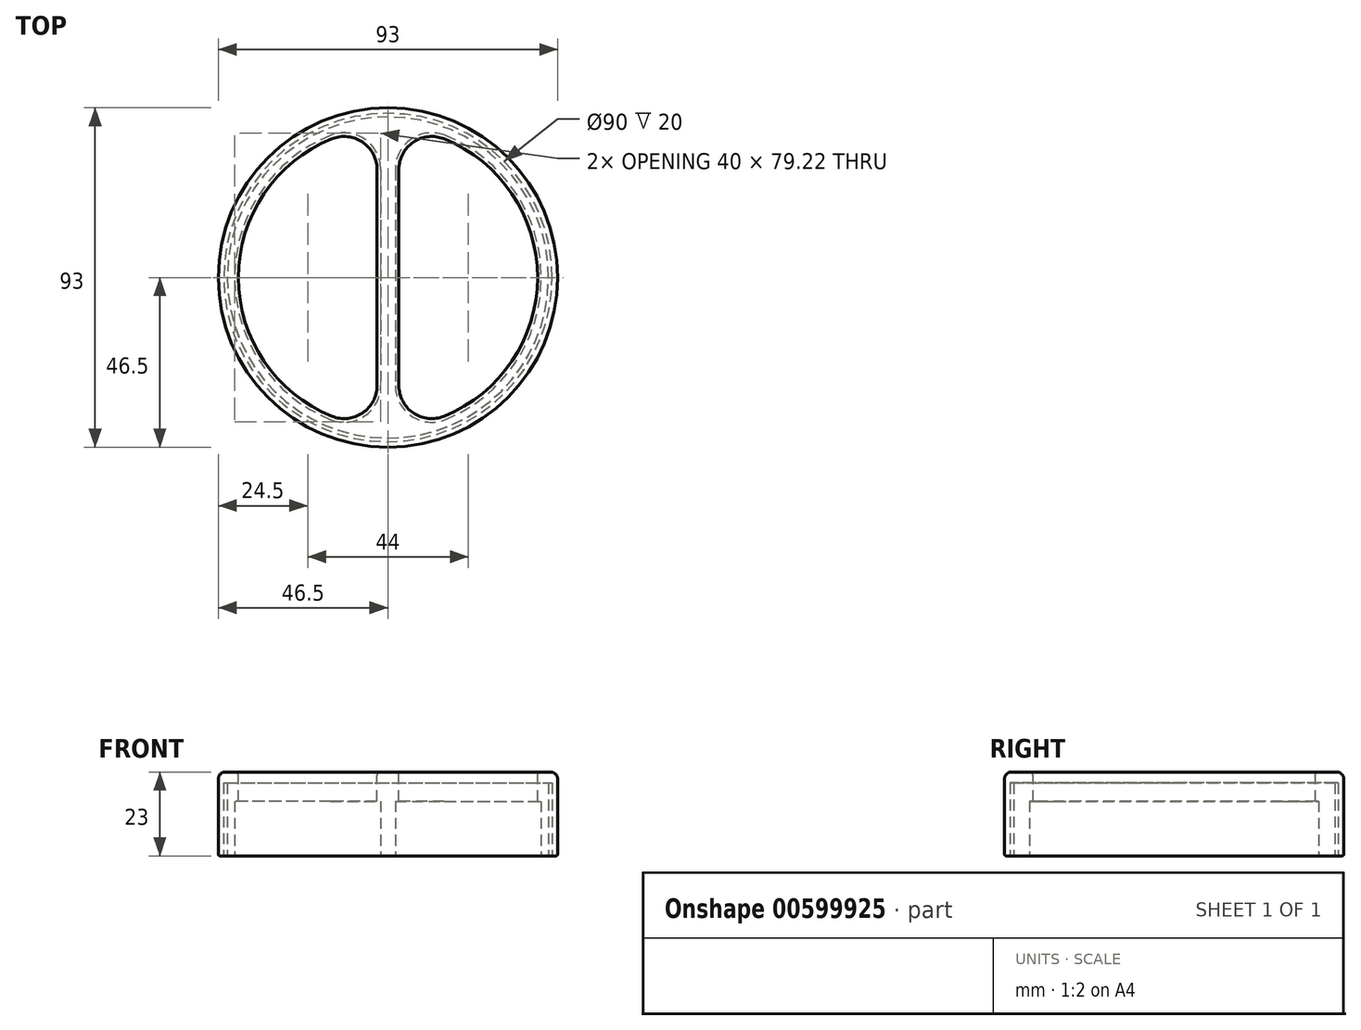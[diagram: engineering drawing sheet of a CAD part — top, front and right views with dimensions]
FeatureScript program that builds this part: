
annotation { "Feature Type Name" : "Feature", "Feature Type Description" : "" }
export const myFeature = defineFeature(function(context is Context, id is Id, definition is map)
    precondition{}
    {
        {
            var Q0;
            Q0=qCreatedBy(makeId("Top.planeOp"),FACE);
            var sketch = newSketch(context, id + "F0", { "sketchPlane" : qUnion([Q0])});
            skCircle(sketch, "E0", {"center": v(0, 0) * mm, "radius": 46.5 * mm});
            skArc(sketch, "E1", {"start": v(-15.38, 38) * mm, "mid": v(-41, 0) * mm, "end": v(-15.38, -38) * mm});
            skLineSegment(sketch, "E2.left", {"start": v(-3, 29.66) * mm, "end": v(-3, -29.66) * mm});
            skLineSegment(sketch, "E2.right", {"start": v(3, 29.66) * mm, "end": v(3, -29.66) * mm});
            skArc(sketch, "E3.trimOffspring", {"start": v(15.38, -38) * mm, "mid": v(41, 0) * mm, "end": v(15.38, 38) * mm});
            skPoint(sketch, "E4.visualSharp", {"position": v(-3, 40.9) * mm});
            skArc(sketch, "E4.filletArc", {"start": v(-3, 29.66) * mm, "mid": v(-6.97, 37.13) * mm, "end": v(-15.38, 38) * mm});
            skPoint(sketch, "E5.visualSharp", {"position": v(3, 40.9) * mm});
            skArc(sketch, "E5.filletArc", {"start": v(15.38, 38) * mm, "mid": v(6.97, 37.13) * mm, "end": v(3, 29.66) * mm});
            skPoint(sketch, "E6.visualSharp", {"position": v(3, -40.9) * mm});
            skArc(sketch, "E6.filletArc", {"start": v(3, -29.66) * mm, "mid": v(6.97, -37.13) * mm, "end": v(15.38, -38) * mm});
            skPoint(sketch, "E7.visualSharp", {"position": v(-3, -40.9) * mm});
            skArc(sketch, "E7.filletArc", {"start": v(-15.37, -38) * mm, "mid": v(-6.97, -37.13) * mm, "end": v(-3, -29.66) * mm});
            skSolve(sketch);
        }
        {
            var Q0;
            Q0=makeQuery(id+"F0.imprint","IMPRINT",FACE,{"disambiguationData":[TD([[makeQuery(id+"F0.imprint","IMPRINT",EDGE,{"derivedFrom":sQuery(id+"F0.wireOp",EDGE,"E0")}),1.0]])]});
            extrude(context, id + "F1", {"entities" : qUnion([Q0]), "oppositeDirection" : true, "depth" : 23 * mm, "offsetDistance" : 25 * mm});
        }
        {
            var Q0;
            Q0=makeQuery(id+"F1.opExtrude","CAP_FACE",FACE,{"disambiguationData":[OSD([sQuery(id+"F0.wireOp",EDGE,"E0"),sQuery(id+"F0.wireOp",EDGE,"E1"),sQuery(id+"F0.wireOp",EDGE,"E2.left"),sQuery(id+"F0.wireOp",EDGE,"E2.right"),sQuery(id+"F0.wireOp",EDGE,"E3.trimOffspring"),sQuery(id+"F0.wireOp",EDGE,"E4.filletArc"),sQuery(id+"F0.wireOp",EDGE,"E5.filletArc"),sQuery(id+"F0.wireOp",EDGE,"E6.filletArc"),sQuery(id+"F0.wireOp",EDGE,"E7.filletArc")])],"isStart":false});
            var sketch = newSketch(context, id + "F2", { "sketchPlane" : qUnion([Q0])});
            skArc(sketch, "E8", {"start": v(15.75, -38.94) * mm, "mid": v(42, 0) * mm, "end": v(15.75, 38.94) * mm});
            skLineSegment(sketch, "E9", {"start": v(2, -29.66) * mm, "end": v(2, 29.66) * mm});
            skLineSegment(sketch, "E10", {"start": v(-2, -29.66) * mm, "end": v(-2, 29.66) * mm});
            skArc(sketch, "E11.trimOffspring", {"start": v(-15.75, 38.94) * mm, "mid": v(-42, 0) * mm, "end": v(-15.75, -38.94) * mm});
            skPoint(sketch, "E12.visualSharp", {"position": v(-2, -41.95) * mm});
            skArc(sketch, "E12.filletArc", {"start": v(-15.75, -38.94) * mm, "mid": v(-6.4, -37.96) * mm, "end": v(-2, -29.66) * mm});
            skPoint(sketch, "E13.visualSharp", {"position": v(2, -41.95) * mm});
            skArc(sketch, "E13.filletArc", {"start": v(2, -29.66) * mm, "mid": v(6.4, -37.96) * mm, "end": v(15.75, -38.94) * mm});
            skPoint(sketch, "E14.visualSharp", {"position": v(2, 41.95) * mm});
            skArc(sketch, "E14.filletArc", {"start": v(15.75, 38.94) * mm, "mid": v(6.4, 37.96) * mm, "end": v(2, 29.66) * mm});
            skPoint(sketch, "E15.visualSharp", {"position": v(-2, 41.95) * mm});
            skArc(sketch, "E15.filletArc", {"start": v(-2, 29.66) * mm, "mid": v(-6.4, 37.96) * mm, "end": v(-15.75, 38.94) * mm});
            skSolve(sketch);
        }
        {
            var Q0;
            Q0=makeQuery(id+"F2.imprint","IMPRINT",FACE,{"disambiguationData":[TD([[makeQuery(id+"F2.imprint","IMPRINT",EDGE,{"derivedFrom":sQuery(id+"F2.wireOp",EDGE,"E10")}),1.0]])]});
            var Q1;
            Q1=makeQuery(id+"F2.imprint","IMPRINT",FACE,{"disambiguationData":[TD([[makeQuery(id+"F2.imprint","IMPRINT",EDGE,{"derivedFrom":sQuery(id+"F2.wireOp",EDGE,"E8")}),1.0]])]});
            extrude(context, id + "F3", {"entities" : qUnion([Q0, Q1]), "operationType" : NewBodyOperationType.REMOVE, "oppositeDirection" : true, "depth" : 15 * mm, "offsetDistance" : 25 * mm});
        }
        {
            var Q0;
            Q0=makeQuery(id+"F1.opExtrude","CAP_EDGE",EDGE,{"disambiguationData":[OSD([sQuery(id+"F0.wireOp",EDGE,"E1")])],"isStart":true});
            var Q1;
            Q1=makeQuery(id+"F1.opExtrude","CAP_EDGE",EDGE,{"disambiguationData":[OSD([sQuery(id+"F0.wireOp",EDGE,"E2.right")])],"isStart":true});
            fillet(context, id + "F4", {"entities" : qUnion([Q0, Q1]), "radius" : 1 * mm, "tangentPropagation" : true, "allowEdgeOverflow" : false});
        }
        {
            var Q0;
            Q0=makeQuery(id+"F1.opExtrude","CAP_FACE",FACE,{"disambiguationData":[OSD([sQuery(id+"F0.wireOp",EDGE,"E0"),sQuery(id+"F0.wireOp",EDGE,"E1"),sQuery(id+"F0.wireOp",EDGE,"E2.left"),sQuery(id+"F0.wireOp",EDGE,"E2.right"),sQuery(id+"F0.wireOp",EDGE,"E3.trimOffspring"),sQuery(id+"F0.wireOp",EDGE,"E4.filletArc"),sQuery(id+"F0.wireOp",EDGE,"E5.filletArc"),sQuery(id+"F0.wireOp",EDGE,"E6.filletArc"),sQuery(id+"F0.wireOp",EDGE,"E7.filletArc")])],"isStart":false});
            var sketch = newSketch(context, id + "F5", { "sketchPlane" : qUnion([Q0])});
            skCircle(sketch, "E16", {"center": v(0, 0) * mm, "radius": 45 * mm});
            skCircle(sketch, "E17", {"center": v(0, 0) * mm, "radius": 44 * mm});
            skSolve(sketch);
        }
        {
            var Q0;
            Q0=makeQuery(id+"F5.imprint","IMPRINT",FACE,{"disambiguationData":[TD([[makeQuery(id+"F5.imprint","IMPRINT",EDGE,{"derivedFrom":sQuery(id+"F5.wireOp",EDGE,"E16")}),1.0]])]});
            extrude(context, id + "F6", {"entities" : qUnion([Q0]), "operationType" : NewBodyOperationType.REMOVE, "oppositeDirection" : true, "depth" : 20 * mm, "offsetDistance" : 25 * mm});
        }
        {
            var Q0;
            Q0=makeQuery(id+"F3.boolean.opBoolean","COPY",EDGE,{"derivedFrom":makeQuery(id+"F3.opExtrude","CAP_EDGE",EDGE,{"disambiguationData":[OSD([sQuery(id+"F2.wireOp",EDGE,"3740ee4f-6de9-44c5-af63-27a4c571abde.3")])],"isStart":true})});
            var Q1;
            Q1=makeQuery(id+"F3.boolean.opBoolean","COPY",EDGE,{"derivedFrom":makeQuery(id+"F3.opExtrude","CAP_EDGE",EDGE,{"disambiguationData":[OSD([sQuery(id+"F2.wireOp",EDGE,"c25a4584-455a-4ff1-a117-f9d434c4c557.0")])],"isStart":true})});
            var Q2;
            Q2=makeQuery(id+"F6.boolean.opBoolean","COPY",EDGE,{"derivedFrom":makeQuery(id+"F6.opExtrude","CAP_EDGE",EDGE,{"disambiguationData":[OSD([sQuery(id+"F5.wireOp",EDGE,"E17")])],"isStart":true})});
            var Q3;
            Q3=makeQuery(id+"F1.opExtrude","CAP_EDGE",EDGE,{"disambiguationData":[OSD([sQuery(id+"F0.wireOp",EDGE,"E0")])],"isStart":false});
            fillet(context, id + "F7", {"entities" : qUnion([Q0, Q1, Q2, Q3]), "radius" : .5 * mm, "tangentPropagation" : true, "allowEdgeOverflow" : false});
        }
        {
            var Q0;
            Q0=makeQuery(id+"F1.opExtrude","CAP_EDGE",EDGE,{"disambiguationData":[OSD([sQuery(id+"F0.wireOp",EDGE,"E0")])],"isStart":true});
            fillet(context, id + "F8", {"entities" : qUnion([Q0]), "radius" : 2 * mm, "tangentPropagation" : true, "allowEdgeOverflow" : false});
        }
    });
